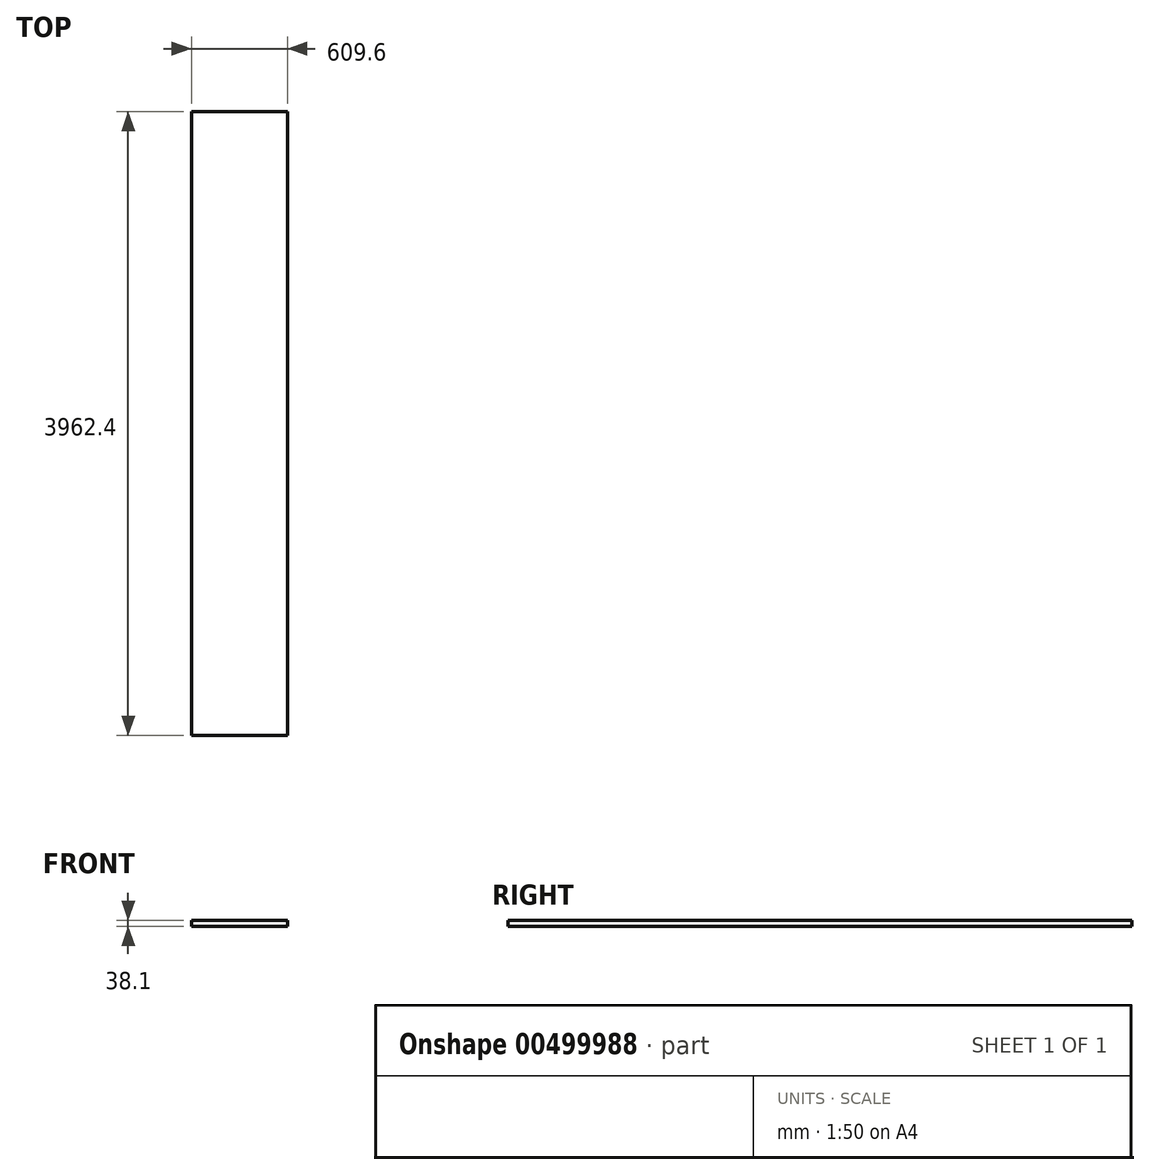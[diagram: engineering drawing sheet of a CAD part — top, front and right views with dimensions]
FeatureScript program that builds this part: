
annotation { "Feature Type Name" : "Feature", "Feature Type Description" : "" }
export const myFeature = defineFeature(function(context is Context, id is Id, definition is map)
    precondition{}
    {
        {
            var Q0;
            Q0=qCreatedBy(makeId("Front.planeOp"),FACE);
            var sketch = newSketch(context, id + "F0", { "sketchPlane" : qUnion([Q0])});
            skLineSegment(sketch, "E0.bottom", {"start": v(-304.8, 19.05) * mm, "end": v(304.8, 19.05) * mm});
            skLineSegment(sketch, "E0.top", {"start": v(-304.8, -19.05) * mm, "end": v(304.8, -19.05) * mm});
            skLineSegment(sketch, "E0.left", {"start": v(-304.8, 19.05) * mm, "end": v(-304.8, -19.05) * mm});
            skLineSegment(sketch, "E0.right", {"start": v(304.8, 19.05) * mm, "end": v(304.8, -19.05) * mm});
            skPoint(sketch, "E0.middle", {"position": v(0, 0) * mm});
            skSolve(sketch);
        }
        {
            var Q0;
            Q0 = qSketchRegion(id + "F0", true);
            extrude(context, id + "F1", {"entities" : qUnion([Q0]), "depth" : 3962.4 * mm, "offsetDistance" : 25.4 * mm});
        }
    });
